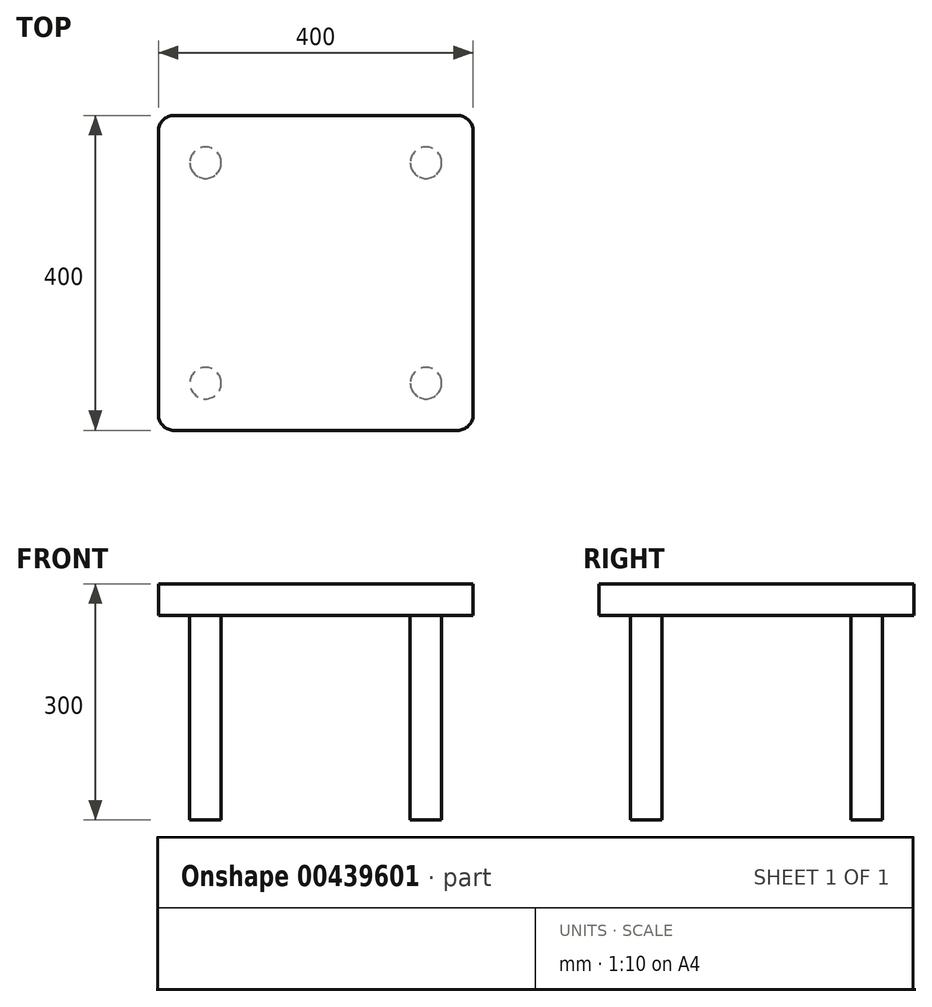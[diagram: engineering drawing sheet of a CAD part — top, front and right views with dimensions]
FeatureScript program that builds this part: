
annotation { "Feature Type Name" : "Feature", "Feature Type Description" : "" }
export const myFeature = defineFeature(function(context is Context, id is Id, definition is map)
    precondition{}
    {
        {
            var Q0;
            Q0=qCreatedBy(makeId("Top.planeOp"),FACE);
            var sketch = newSketch(context, id + "F0", { "sketchPlane" : qUnion([Q0])});
            skLineSegment(sketch, "E0.bottom", {"start": v(-175.12, 231.24) * mm, "end": v(184.88, 231.24) * mm});
            skLineSegment(sketch, "E0.top", {"start": v(-175.12, -168.76) * mm, "end": v(184.88, -168.76) * mm});
            skLineSegment(sketch, "E0.left", {"start": v(-195.12, 211.24) * mm, "end": v(-195.12, -148.76) * mm});
            skLineSegment(sketch, "E0.right", {"start": v(204.88, 211.24) * mm, "end": v(204.88, -148.76) * mm});
            skPoint(sketch, "E1.visualSharp", {"position": v(204.88, 231.24) * mm});
            skArc(sketch, "E1.filletArc", {"start": v(204.88, 211.24) * mm, "mid": v(199.02, 225.38) * mm, "end": v(184.88, 231.24) * mm});
            skPoint(sketch, "E2.visualSharp", {"position": v(204.88, -168.76) * mm});
            skArc(sketch, "E2.filletArc", {"start": v(184.88, -168.76) * mm, "mid": v(199.02, -162.9) * mm, "end": v(204.88, -148.76) * mm});
            skPoint(sketch, "E3.visualSharp", {"position": v(-195.12, -168.76) * mm});
            skArc(sketch, "E3.filletArc", {"start": v(-195.12, -148.76) * mm, "mid": v(-189.26, -162.9) * mm, "end": v(-175.12, -168.76) * mm});
            skPoint(sketch, "E4.visualSharp", {"position": v(-195.12, 231.24) * mm});
            skArc(sketch, "E4.filletArc", {"start": v(-175.12, 231.24) * mm, "mid": v(-189.26, 225.38) * mm, "end": v(-195.12, 211.24) * mm});
            skSolve(sketch);
        }
        {
            var Q0;
            Q0=makeQuery(id+"F0.imprint","IMPRINT",FACE,{"disambiguationData":[TD([[makeQuery(id+"F0.imprint","IMPRINT",EDGE,{"derivedFrom":sQuery(id+"F0.wireOp",EDGE,"E0.bottom")}),-1.0]])]});
            extrude(context, id + "F1", {"entities" : qUnion([Q0]), "depth" : 40 * mm});
        }
        {
            var Q0;
            Q0=makeQuery(id+"F1.opExtrude","CAP_FACE",FACE,{"disambiguationData":[OSD([sQuery(id+"F0.wireOp",EDGE,"E0.bottom"),sQuery(id+"F0.wireOp",EDGE,"E0.top"),sQuery(id+"F0.wireOp",EDGE,"E0.left"),sQuery(id+"F0.wireOp",EDGE,"E0.right"),sQuery(id+"F0.wireOp",EDGE,"E1.filletArc"),sQuery(id+"F0.wireOp",EDGE,"E2.filletArc"),sQuery(id+"F0.wireOp",EDGE,"E3.filletArc"),sQuery(id+"F0.wireOp",EDGE,"E4.filletArc")])],"isStart":true});
            var sketch = newSketch(context, id + "F2", { "sketchPlane" : qUnion([Q0])});
            skLineSegment(sketch, "E5.bottom", {"start": v(-135.12, -151.24) * mm, "end": v(-135.12, -151.24) * mm});
            skLineSegment(sketch, "E5.top", {"start": v(-135.12, -191.24) * mm, "end": v(-135.12, -191.24) * mm});
            skLineSegment(sketch, "E5.left", {"start": v(-155.12, -171.24) * mm, "end": v(-155.12, -171.24) * mm});
            skLineSegment(sketch, "E5.right", {"start": v(-115.12, -171.24) * mm, "end": v(-115.12, -171.24) * mm});
            skLineSegment(sketch, "E6.bottom", {"start": v(144.88, -151.24) * mm, "end": v(144.88, -151.24) * mm});
            skLineSegment(sketch, "E6.top", {"start": v(144.88, -191.24) * mm, "end": v(144.88, -191.24) * mm});
            skLineSegment(sketch, "E6.left", {"start": v(124.88, -171.24) * mm, "end": v(124.88, -171.24) * mm});
            skLineSegment(sketch, "E6.right", {"start": v(164.88, -171.24) * mm, "end": v(164.88, -171.24) * mm});
            skLineSegment(sketch, "E7.bottom", {"start": v(144.88, 128.76) * mm, "end": v(144.88, 128.76) * mm});
            skLineSegment(sketch, "E7.top", {"start": v(144.88, 88.76) * mm, "end": v(144.88, 88.76) * mm});
            skLineSegment(sketch, "E7.left", {"start": v(124.88, 108.76) * mm, "end": v(124.88, 108.76) * mm});
            skLineSegment(sketch, "E7.right", {"start": v(164.88, 108.76) * mm, "end": v(164.88, 108.76) * mm});
            skLineSegment(sketch, "E8.bottom", {"start": v(-135.12, 128.76) * mm, "end": v(-135.12, 128.76) * mm});
            skLineSegment(sketch, "E8.top", {"start": v(-135.12, 88.76) * mm, "end": v(-135.12, 88.76) * mm});
            skLineSegment(sketch, "E8.left", {"start": v(-155.12, 108.76) * mm, "end": v(-155.12, 108.76) * mm});
            skLineSegment(sketch, "E8.right", {"start": v(-115.12, 108.76) * mm, "end": v(-115.12, 108.76) * mm});
            skPoint(sketch, "E9.visualSharp", {"position": v(-115.12, 128.76) * mm});
            skArc(sketch, "E9.filletArc", {"start": v(-115.12, 108.76) * mm, "mid": v(-120.98, 122.9) * mm, "end": v(-135.12, 128.76) * mm});
            skPoint(sketch, "E10.visualSharp", {"position": v(-155.12, 128.76) * mm});
            skArc(sketch, "E10.filletArc", {"start": v(-135.12, 128.76) * mm, "mid": v(-149.26, 122.9) * mm, "end": v(-155.12, 108.76) * mm});
            skPoint(sketch, "E11.visualSharp", {"position": v(-155.12, 88.76) * mm});
            skArc(sketch, "E11.filletArc", {"start": v(-155.12, 108.76) * mm, "mid": v(-149.26, 94.62) * mm, "end": v(-135.12, 88.76) * mm});
            skPoint(sketch, "E12.visualSharp", {"position": v(-115.12, 88.76) * mm});
            skArc(sketch, "E12.filletArc", {"start": v(-135.12, 88.76) * mm, "mid": v(-120.98, 94.62) * mm, "end": v(-115.12, 108.76) * mm});
            skPoint(sketch, "E13.visualSharp", {"position": v(-115.12, -151.24) * mm});
            skArc(sketch, "E13.filletArc", {"start": v(-115.12, -171.24) * mm, "mid": v(-120.98, -157.1) * mm, "end": v(-135.12, -151.24) * mm});
            skPoint(sketch, "E14.visualSharp", {"position": v(-115.12, -191.24) * mm});
            skArc(sketch, "E14.filletArc", {"start": v(-135.12, -191.24) * mm, "mid": v(-120.98, -185.38) * mm, "end": v(-115.12, -171.24) * mm});
            skPoint(sketch, "E15.visualSharp", {"position": v(-155.12, -191.24) * mm});
            skArc(sketch, "E15.filletArc", {"start": v(-155.12, -171.24) * mm, "mid": v(-149.26, -185.38) * mm, "end": v(-135.12, -191.24) * mm});
            skPoint(sketch, "E16.visualSharp", {"position": v(-155.12, -151.24) * mm});
            skArc(sketch, "E16.filletArc", {"start": v(-135.12, -151.24) * mm, "mid": v(-149.26, -157.1) * mm, "end": v(-155.12, -171.24) * mm});
            skPoint(sketch, "E17.visualSharp", {"position": v(124.88, -151.24) * mm});
            skArc(sketch, "E17.filletArc", {"start": v(144.88, -151.24) * mm, "mid": v(130.74, -157.1) * mm, "end": v(124.88, -171.24) * mm});
            skPoint(sketch, "E18.visualSharp", {"position": v(124.88, -191.24) * mm});
            skArc(sketch, "E18.filletArc", {"start": v(124.88, -171.24) * mm, "mid": v(130.74, -185.38) * mm, "end": v(144.88, -191.24) * mm});
            skPoint(sketch, "E19.visualSharp", {"position": v(164.88, -191.24) * mm});
            skArc(sketch, "E19.filletArc", {"start": v(144.88, -191.24) * mm, "mid": v(159.02, -185.38) * mm, "end": v(164.88, -171.24) * mm});
            skPoint(sketch, "E20.visualSharp", {"position": v(164.88, -151.24) * mm});
            skArc(sketch, "E20.filletArc", {"start": v(164.88, -171.24) * mm, "mid": v(159.02, -157.1) * mm, "end": v(144.88, -151.24) * mm});
            skPoint(sketch, "E21.visualSharp", {"position": v(124.88, 88.76) * mm});
            skArc(sketch, "E21.filletArc", {"start": v(124.88, 108.76) * mm, "mid": v(130.74, 94.62) * mm, "end": v(144.88, 88.76) * mm});
            skPoint(sketch, "E22.visualSharp", {"position": v(164.88, 88.76) * mm});
            skArc(sketch, "E22.filletArc", {"start": v(144.88, 88.76) * mm, "mid": v(159.02, 94.62) * mm, "end": v(164.88, 108.76) * mm});
            skPoint(sketch, "E23.visualSharp", {"position": v(124.88, 128.76) * mm});
            skArc(sketch, "E23.filletArc", {"start": v(144.88, 128.76) * mm, "mid": v(130.74, 122.9) * mm, "end": v(124.88, 108.76) * mm});
            skPoint(sketch, "E24.visualSharp", {"position": v(164.88, 128.76) * mm});
            skArc(sketch, "E24.filletArc", {"start": v(164.88, 108.76) * mm, "mid": v(159.02, 122.9) * mm, "end": v(144.88, 128.76) * mm});
            skSolve(sketch);
        }
        {
            var Q0;
            Q0=makeQuery(id+"F2.imprint","IMPRINT",FACE,{"disambiguationData":[TD([[makeQuery(id+"F2.imprint","IMPRINT",EDGE,{"derivedFrom":sQuery(id+"F2.wireOp",EDGE,"E13.filletArc")}),1.0]])]});
            var Q1;
            Q1=makeQuery(id+"F2.imprint","IMPRINT",FACE,{"disambiguationData":[TD([[makeQuery(id+"F2.imprint","IMPRINT",EDGE,{"derivedFrom":sQuery(id+"F2.wireOp",EDGE,"E9.filletArc")}),1.0]])]});
            var Q2;
            Q2=makeQuery(id+"F2.imprint","IMPRINT",FACE,{"disambiguationData":[TD([[makeQuery(id+"F2.imprint","IMPRINT",EDGE,{"derivedFrom":sQuery(id+"F2.wireOp",EDGE,"E21.filletArc")}),1.0]])]});
            var Q3;
            Q3=makeQuery(id+"F2.imprint","IMPRINT",FACE,{"disambiguationData":[TD([[makeQuery(id+"F2.imprint","IMPRINT",EDGE,{"derivedFrom":sQuery(id+"F2.wireOp",EDGE,"E17.filletArc")}),1.0]])]});
            extrude(context, id + "F3", {"entities" : qUnion([Q0, Q1, Q2, Q3]), "operationType" : NewBodyOperationType.ADD, "depth" : 260 * mm});
        }
    });
